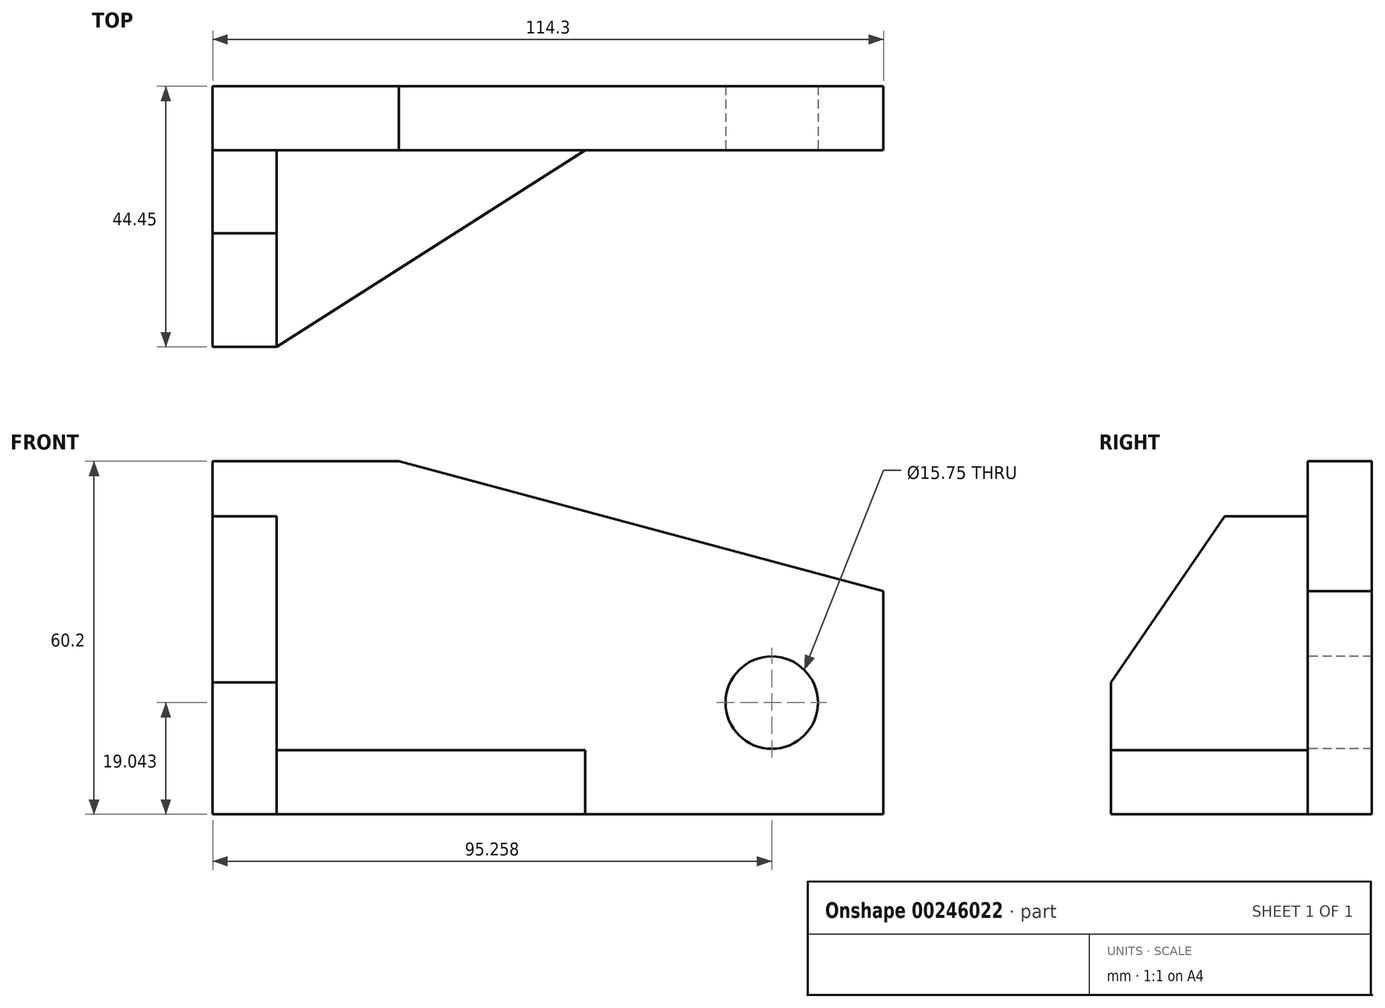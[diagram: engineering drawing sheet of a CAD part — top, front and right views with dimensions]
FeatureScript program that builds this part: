
annotation { "Feature Type Name" : "Feature", "Feature Type Description" : "" }
export const myFeature = defineFeature(function(context is Context, id is Id, definition is map)
    precondition{}
    {
        {
            var Q0;
            Q0=qCreatedBy(makeId("Front.planeOp"),FACE);
            var sketch = newSketch(context, id + "F0", { "sketchPlane" : qUnion([Q0])});
            skLineSegment(sketch, "E0", {"start": v(-55.54, 30.44) * mm, "end": v(-55.54, -29.76) * mm});
            skLineSegment(sketch, "E1", {"start": v(-55.54, -29.76) * mm, "end": v(58.76, -29.76) * mm});
            skLineSegment(sketch, "E2", {"start": v(-55.54, 30.44) * mm, "end": v(-23.8, 30.44) * mm});
            skLineSegment(sketch, "E3", {"start": v(58.76, 8.32) * mm, "end": v(58.76, -29.76) * mm});
            skLineSegment(sketch, "E4", {"start": v(-23.8, 30.44) * mm, "end": v(58.76, 8.32) * mm});
            skPoint(sketch, "E5.orphan", {"position": v(58.76, 30.44) * mm});
            skSolve(sketch);
        }
        {
            var Q0;
            Q0 = qSketchRegion(id + "F0", true);
            extrude(context, id + "F1", {"entities" : qUnion([Q0]), "depth" : 10.92 * mm});
        }
        {
            var Q0;
            Q0=makeQuery(id+"F1.opExtrude","CAP_FACE",FACE,{"disambiguationData":[OSD([sQuery(id+"F0.wireOp",EDGE,"E0"),sQuery(id+"F0.wireOp",EDGE,"E1"),sQuery(id+"F0.wireOp",EDGE,"E3"),sQuery(id+"F0.wireOp",EDGE,"E2"),sQuery(id+"F0.wireOp",EDGE,"E4")])],"isStart":false});
            var sketch = newSketch(context, id + "F2", { "sketchPlane" : qUnion([Q0])});
            skLineSegment(sketch, "E6", {"start": v(-55.54, 21.04) * mm, "end": v(-44.62, 21.04) * mm});
            skLineSegment(sketch, "E7", {"start": v(-44.62, 21.04) * mm, "end": v(-44.62, -18.83) * mm});
            skLineSegment(sketch, "E8", {"start": v(-44.62, -18.83) * mm, "end": v(7.96, -18.83) * mm});
            skLineSegment(sketch, "E9", {"start": v(7.96, -18.83) * mm, "end": v(7.96, -29.76) * mm});
            skLineSegment(sketch, "E10", {"start": v(-55.54, 21.04) * mm, "end": v(-55.54, -29.76) * mm});
            skLineSegment(sketch, "E11", {"start": v(-55.54, -29.76) * mm, "end": v(7.96, -29.76) * mm});
            skSolve(sketch);
        }
        {
            var Q0;
            Q0=makeQuery(id+"F2.imprint","IMPRINT",FACE,{"disambiguationData":[TD([[makeQuery(id+"F2.imprint","IMPRINT",EDGE,{"derivedFrom":sQuery(id+"F2.wireOp",EDGE,"E6")}),-1.0]])]});
            extrude(context, id + "F3", {"entities" : qUnion([Q0]), "operationType" : NewBodyOperationType.ADD, "depth" : 33.53 * mm});
        }
        {
            var Q0;
            Q0=makeQuery(id+"F3.boolean.opBoolean","MERGE",FACE,{"derivedFrom":[makeQuery(id+"F1.opExtrude","SWEPT_FACE",FACE,{"disambiguationData":[OSD([sQuery(id+"F0.wireOp",EDGE,"E0")])]}),makeQuery(id+"F3.opExtrude","SWEPT_FACE",FACE,{"disambiguationData":[OSD([sQuery(id+"F2.wireOp",EDGE,"E10")])]})]});
            var sketch = newSketch(context, id + "F4", { "sketchPlane" : qUnion([Q0])});
            skLineSegment(sketch, "E12", {"start": v(44.45, -29.76) * mm, "end": v(44.45, -7.28) * mm});
            skLineSegment(sketch, "E13", {"start": v(44.45, -7.28) * mm, "end": v(25.08, 21.04) * mm});
            skLineSegment(sketch, "E14", {"start": v(25.08, 21.04) * mm, "end": v(44.45, 21.04) * mm});
            skLineSegment(sketch, "E15", {"start": v(44.35, 20.77) * mm, "end": v(44.45, -7.28) * mm});
            skSolve(sketch);
        }
        {
            var Q0;
            {var subQ0=sQuery(id+"F4.wireOp",EDGE,"E13");Q0=makeQuery(id+"F4.imprint","IMPRINT",FACE,{"disambiguationData":[TD([[makeQuery(id+"F4.imprint","IMPRINT",EDGE,{"derivedFrom":subQ0}),-1.0]])]});}
            extrude(context, id + "F5", {"entities" : qUnion([Q0]), "operationType" : NewBodyOperationType.REMOVE, "endBound" : BoundingType.THROUGH_ALL, "oppositeDirection" : true, "depth" : 25.4 * mm});
        }
        {
            var Q0;
            Q0=makeQuery(id+"F3.opExtrude","SWEPT_FACE",FACE,{"disambiguationData":[OSD([sQuery(id+"F2.wireOp",EDGE,"E8")])]});
            var sketch = newSketch(context, id + "F6", { "sketchPlane" : qUnion([Q0])});
            skLineSegment(sketch, "E16", {"start": v(7.96, -10.92) * mm, "end": v(-44.62, -44.45) * mm});
            skLineSegment(sketch, "E17", {"start": v(7.96, -10.92) * mm, "end": v(7.96, -44.45) * mm});
            skLineSegment(sketch, "E18", {"start": v(7.96, -44.45) * mm, "end": v(-44.62, -44.45) * mm});
            skSolve(sketch);
        }
        {
            var Q0;
            Q0=makeQuery(id+"F6.imprint","IMPRINT",FACE,{"disambiguationData":[TD([[makeQuery(id+"F6.imprint","IMPRINT",EDGE,{"derivedFrom":sQuery(id+"F6.wireOp",EDGE,"E16")}),1.0]])]});
            extrude(context, id + "F7", {"entities" : qUnion([Q0]), "operationType" : NewBodyOperationType.REMOVE, "endBound" : BoundingType.THROUGH_ALL, "oppositeDirection" : true, "depth" : 25.4 * mm});
        }
        {
            var Q0;
            Q0=makeQuery(id+"F1.opExtrude","CAP_FACE",FACE,{"disambiguationData":[OSD([sQuery(id+"F0.wireOp",EDGE,"E0"),sQuery(id+"F0.wireOp",EDGE,"E1"),sQuery(id+"F0.wireOp",EDGE,"E3"),sQuery(id+"F0.wireOp",EDGE,"E2"),sQuery(id+"F0.wireOp",EDGE,"E4")])],"isStart":false});
            var sketch = newSketch(context, id + "F8", { "sketchPlane" : qUnion([Q0])});
            skLineSegment(sketch, "E19", {"start": v(58.76, -10.72) * mm, "end": v(39.72, -10.72) * mm, "construction": true});
            skLineSegment(sketch, "E20", {"start": v(39.72, -10.72) * mm, "end": v(39.72, -29.76) * mm, "construction": true});
            skCircle(sketch, "E21", {"center": v(39.72, -10.72) * mm, "radius": 7.87 * mm});
            skSolve(sketch);
        }
        {
            var Q0;
            Q0=makeQuery(id+"F8.imprint","IMPRINT",FACE,{"disambiguationData":[TD([[makeQuery(id+"F8.imprint","IMPRINT",EDGE,{"derivedFrom":sQuery(id+"F8.wireOp",EDGE,"E21")}),1.0]])]});
            extrude(context, id + "F9", {"entities" : qUnion([Q0]), "operationType" : NewBodyOperationType.REMOVE, "endBound" : BoundingType.THROUGH_ALL, "oppositeDirection" : true, "depth" : 25.4 * mm});
        }
    });
